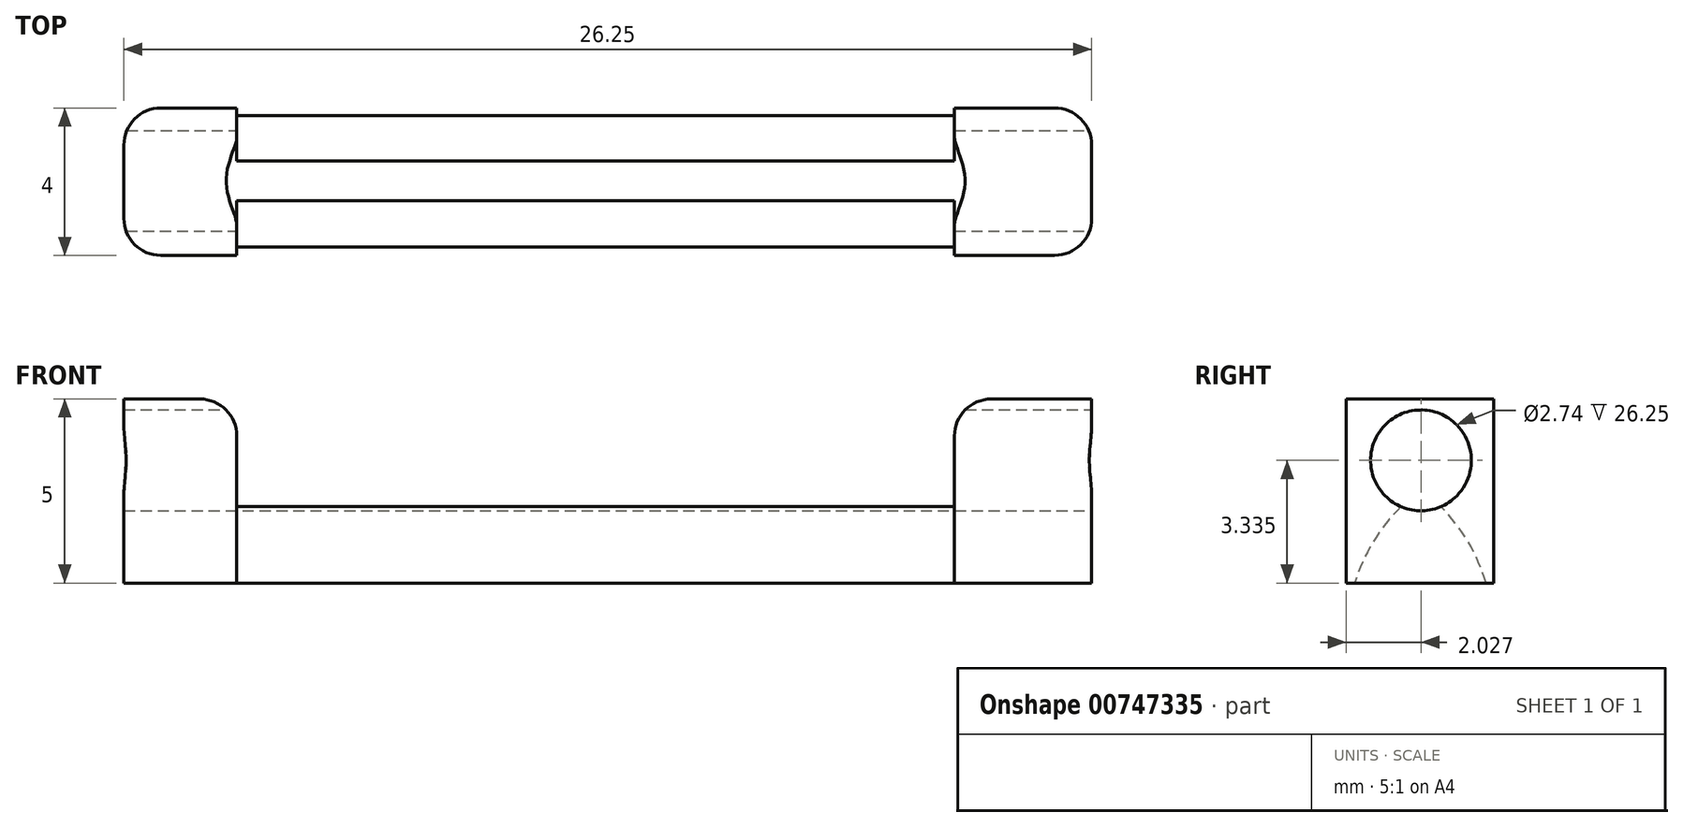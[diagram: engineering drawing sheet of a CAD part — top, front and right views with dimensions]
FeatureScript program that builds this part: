
annotation { "Feature Type Name" : "Feature", "Feature Type Description" : "" }
export const myFeature = defineFeature(function(context is Context, id is Id, definition is map)
    precondition{}
    {
        {
            var Q0;
            Q0=qCreatedBy(makeId("Top.planeOp"),FACE);
            var sketch = newSketch(context, id + "F0", { "sketchPlane" : qUnion([Q0])});
            skLineSegment(sketch, "E0.bottom", {"start": v(-14.55, 0.17) * mm, "end": v(11.7, 0.17) * mm});
            skLineSegment(sketch, "E0.top", {"start": v(-14.55, -3.83) * mm, "end": v(11.7, -3.83) * mm});
            skLineSegment(sketch, "E0.left", {"start": v(-14.55, 0.17) * mm, "end": v(-14.55, -3.83) * mm});
            skLineSegment(sketch, "E0.right", {"start": v(11.7, 0.17) * mm, "end": v(11.7, -3.83) * mm});
            skSolve(sketch);
        }
        {
            var Q0;
            Q0=makeQuery(id+"F0.imprint","IMPRINT",FACE,{"disambiguationData":[TD([[makeQuery(id+"F0.imprint","IMPRINT",EDGE,{"derivedFrom":sQuery(id+"F0.wireOp",EDGE,"E0.bottom")}),-1.0]])]});
            extrude(context, id + "F1", {"entities" : qUnion([Q0]), "depth" : 5 * mm, "offsetDistance" : 25 * mm});
        }
        {
            var Q0;
            Q0=qCreatedBy(makeId("Front.planeOp"),FACE);
            var sketch = newSketch(context, id + "F2", { "sketchPlane" : qUnion([Q0])});
            skLineSegment(sketch, "E1.bottom", {"start": v(-11.48, 6.67) * mm, "end": v(7.98, 6.67) * mm});
            skLineSegment(sketch, "E1.top", {"start": v(-11.48, 2.08) * mm, "end": v(7.98, 2.08) * mm});
            skLineSegment(sketch, "E1.left", {"start": v(-11.48, 6.67) * mm, "end": v(-11.48, 2.08) * mm});
            skLineSegment(sketch, "E1.right", {"start": v(7.98, 6.67) * mm, "end": v(7.98, 2.08) * mm});
            skSolve(sketch);
        }
        {
            var Q0;
            Q0 = qSketchRegion(id + "F2", true);
            extrude(context, id + "F3", {"entities" : qUnion([Q0]), "operationType" : NewBodyOperationType.REMOVE, "depth" : 43.3 * mm, "offsetDistance" : 25 * mm});
        }
        {
            var Q0;
            Q0 = qSketchRegion(id + "F2", true);
            extrude(context, id + "F4", {"entities" : qUnion([Q0]), "operationType" : NewBodyOperationType.REMOVE, "oppositeDirection" : true, "depth" : 52.6 * mm, "offsetDistance" : 25 * mm});
        }
        {
            var Q0;
            Q0=qCreatedBy(makeId("Right.planeOp"),FACE);
            var sketch = newSketch(context, id + "F5", { "sketchPlane" : qUnion([Q0])});
            skCircle(sketch, "E2", {"center": v(-1.8, 3.33) * mm, "radius": 1.37 * mm});
            skSolve(sketch);
        }
        {
            var Q0;
            Q0=makeQuery(id+"F5.imprint","IMPRINT",FACE,{"disambiguationData":[TD([[makeQuery(id+"F5.imprint","IMPRINT",EDGE,{"derivedFrom":sQuery(id+"F5.wireOp",EDGE,"E2")}),1.0]])]});
            extrude(context, id + "F6", {"entities" : qUnion([Q0]), "operationType" : NewBodyOperationType.REMOVE, "oppositeDirection" : true, "depth" : 25 * mm, "offsetDistance" : 25 * mm});
        }
        {
            var Q0;
            Q0 = qSketchRegion(id + "F5", true);
            extrude(context, id + "F7", {"entities" : qUnion([Q0]), "operationType" : NewBodyOperationType.REMOVE, "depth" : 21.1 * mm, "offsetDistance" : 25 * mm});
        }
        {
            var Q0;
            Q0=makeQuery(id+"F1.opExtrude","SWEPT_EDGE",EDGE,{"disambiguationData":[OSD([sQuery(id+"F0.wireOp",EDGE,"E0.bottom"),sQuery(id+"F0.wireOp",EDGE,"E0.right")])]});
            fillet(context, id + "F8", {"entities" : qUnion([Q0]), "radius" : 1 * mm, "tangentPropagation" : true, "allowEdgeOverflow" : false});
        }
        {
            var Q0;
            Q0=makeQuery(id+"F1.opExtrude","SWEPT_EDGE",EDGE,{"disambiguationData":[OSD([sQuery(id+"F0.wireOp",EDGE,"E0.bottom"),sQuery(id+"F0.wireOp",EDGE,"E0.left")])]});
            fillet(context, id + "F9", {"entities" : qUnion([Q0]), "radius" : 1 * mm, "tangentPropagation" : true, "allowEdgeOverflow" : false});
        }
        {
            var Q0;
            Q0=makeQuery(id+"F1.opExtrude","SWEPT_EDGE",EDGE,{"disambiguationData":[OSD([sQuery(id+"F0.wireOp",EDGE,"E0.top"),sQuery(id+"F0.wireOp",EDGE,"E0.right")])]});
            var Q1;
            Q1=makeQuery(id+"F1.opExtrude","SWEPT_EDGE",EDGE,{"disambiguationData":[OSD([sQuery(id+"F0.wireOp",EDGE,"E0.top"),sQuery(id+"F0.wireOp",EDGE,"E0.left")])]});
            fillet(context, id + "F10", {"entities" : qUnion([Q0, Q1]), "radius" : 1 * mm, "tangentPropagation" : true, "allowEdgeOverflow" : false});
        }
        {
            var Q0;
            Q0=makeQuery(id+"F4.boolean.opBoolean","INTERSECT",EDGE,{"derivedFrom":[makeQuery(id+"F1.opExtrude","SWEPT_FACE",FACE,{"disambiguationData":[OSD([sQuery(id+"F0.wireOp",EDGE,"E0.bottom")])]}),makeQuery(id+"F4.opExtrude","SWEPT_FACE",FACE,{"disambiguationData":[OSD([sQuery(id+"F2.wireOp",EDGE,"E1.top")])]})]});
            var Q1;
            Q1=makeQuery(id+"F3.boolean.opBoolean","INTERSECT",EDGE,{"derivedFrom":[makeQuery(id+"F1.opExtrude","SWEPT_FACE",FACE,{"disambiguationData":[OSD([sQuery(id+"F0.wireOp",EDGE,"E0.top")])]}),makeQuery(id+"F3.opExtrude","SWEPT_FACE",FACE,{"disambiguationData":[OSD([sQuery(id+"F2.wireOp",EDGE,"E1.top")])]})]});
            fillet(context, id + "F11", {"entities" : qUnion([Q0, Q1]), "radius" : 5 * mm, "tangentPropagation" : true, "allowEdgeOverflow" : false});
        }
        {
            var Q0;
            Q0=makeQuery(id+"F4.boolean.opBoolean","INTERSECT",EDGE,{"derivedFrom":[makeQuery(id+"F1.opExtrude","CAP_FACE",FACE,{"disambiguationData":[OSD([sQuery(id+"F0.wireOp",EDGE,"E0.bottom"),sQuery(id+"F0.wireOp",EDGE,"E0.top"),sQuery(id+"F0.wireOp",EDGE,"E0.left"),sQuery(id+"F0.wireOp",EDGE,"E0.right")])],"isStart":false}),makeQuery(id+"F4.opExtrude","SWEPT_FACE",FACE,{"disambiguationData":[OSD([sQuery(id+"F2.wireOp",EDGE,"E1.left")])]})]});
            var Q1;
            Q1=makeQuery(id+"F4.boolean.opBoolean","INTERSECT",EDGE,{"derivedFrom":[makeQuery(id+"F1.opExtrude","CAP_FACE",FACE,{"disambiguationData":[OSD([sQuery(id+"F0.wireOp",EDGE,"E0.bottom"),sQuery(id+"F0.wireOp",EDGE,"E0.top"),sQuery(id+"F0.wireOp",EDGE,"E0.left"),sQuery(id+"F0.wireOp",EDGE,"E0.right")])],"isStart":false}),makeQuery(id+"F4.opExtrude","SWEPT_FACE",FACE,{"disambiguationData":[OSD([sQuery(id+"F2.wireOp",EDGE,"E1.right")])]})]});
            fillet(context, id + "F12", {"entities" : qUnion([Q0, Q1]), "radius" : 1 * mm, "tangentPropagation" : true, "allowEdgeOverflow" : false});
        }
    });
